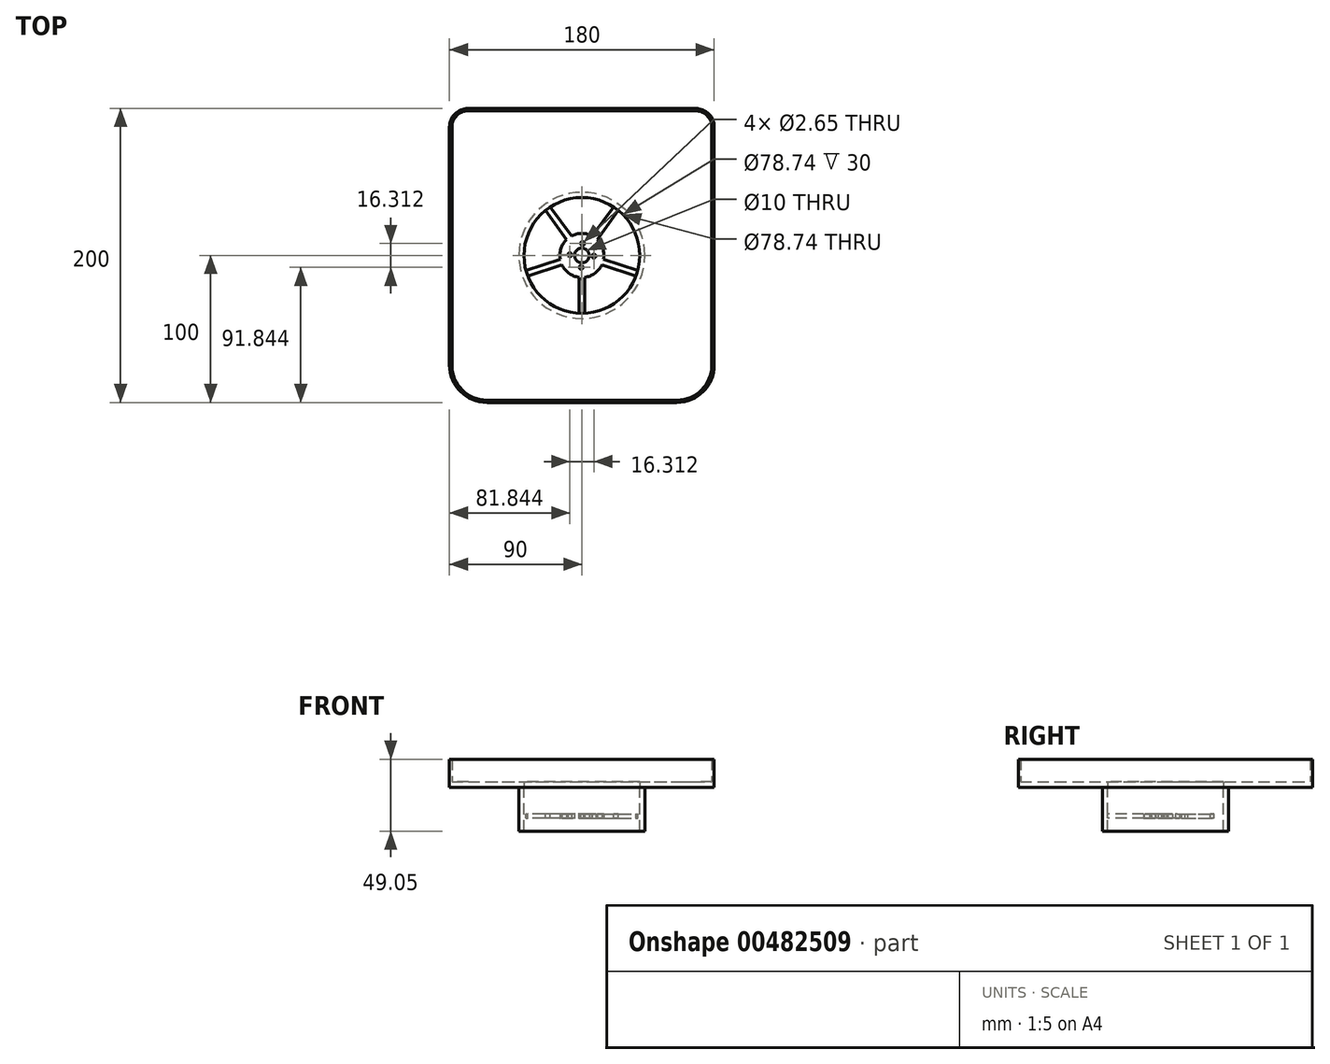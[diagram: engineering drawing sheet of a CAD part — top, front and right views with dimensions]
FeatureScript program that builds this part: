
annotation { "Feature Type Name" : "Feature", "Feature Type Description" : "" }
export const myFeature = defineFeature(function(context is Context, id is Id, definition is map)
    precondition{}
    {
        {
            var Q0;
            Q0=qCreatedBy(makeId("Top.planeOp"),FACE);
            var sketch = newSketch(context, id + "F0", { "sketchPlane" : qUnion([Q0])});
            skLineSegment(sketch, "E0.bottom", {"start": v(25.4, 0) * mm, "end": v(154.6, 0) * mm});
            skLineSegment(sketch, "E0.top", {"start": v(12.7, 200) * mm, "end": v(167.3, 200) * mm});
            skLineSegment(sketch, "E0.left", {"start": v(0, 25.4) * mm, "end": v(0, 187.3) * mm});
            skLineSegment(sketch, "E0.right", {"start": v(180, 25.4) * mm, "end": v(180, 187.3) * mm});
            skPoint(sketch, "E1.visualSharp", {"position": v(0, 0) * mm});
            skArc(sketch, "E1.filletArc", {"start": v(0, 25.4) * mm, "mid": v(7.44, 7.44) * mm, "end": v(25.4, 0) * mm});
            skPoint(sketch, "E2.visualSharp", {"position": v(180, 0) * mm});
            skArc(sketch, "E2.filletArc", {"start": v(154.6, 0) * mm, "mid": v(172.56, 7.44) * mm, "end": v(180, 25.4) * mm});
            skCircle(sketch, "E3", {"center": v(90, 100) * mm, "radius": 39.37 * mm});
            skPoint(sketch, "E4.visualSharp", {"position": v(0, 200) * mm});
            skArc(sketch, "E4.filletArc", {"start": v(12.7, 200) * mm, "mid": v(3.72, 196.28) * mm, "end": v(0, 187.3) * mm});
            skPoint(sketch, "E5.visualSharp", {"position": v(180, 200) * mm});
            skArc(sketch, "E5.filletArc", {"start": v(180, 187.3) * mm, "mid": v(176.28, 196.28) * mm, "end": v(167.3, 200) * mm});
            skSolve(sketch);
        }
        {
            var Q0;
            Q0 = qSketchRegion(id + "F0", true);
            extrude(context, id + "F1", {"entities" : qUnion([Q0]), "depth" : 3.8 * mm});
        }
        {
            var Q0;
            Q0=makeQuery(id+"F1.opExtrude","CAP_FACE",FACE,{"disambiguationData":[OSD([sQuery(id+"F0.wireOp",EDGE,"E0.bottom"),sQuery(id+"F0.wireOp",EDGE,"E0.top"),sQuery(id+"F0.wireOp",EDGE,"E0.left"),sQuery(id+"F0.wireOp",EDGE,"E0.right"),sQuery(id+"F0.wireOp",EDGE,"E1.filletArc"),sQuery(id+"F0.wireOp",EDGE,"E2.filletArc"),sQuery(id+"F0.wireOp",EDGE,"E3"),sQuery(id+"F0.wireOp",EDGE,"E4.filletArc"),sQuery(id+"F0.wireOp",EDGE,"E5.filletArc")])],"isStart":false});
            var sketch = newSketch(context, id + "F2", { "sketchPlane" : qUnion([Q0])});
            skArc(sketch, "E6.0", {"start": v(154.6, 1.6) * mm, "mid": v(171.43, 8.57) * mm, "end": v(178.4, 25.4) * mm});
            skLineSegment(sketch, "E6.1", {"start": v(25.4, 1.6) * mm, "end": v(154.6, 1.6) * mm});
            skLineSegment(sketch, "E6.2", {"start": v(178.4, 25.4) * mm, "end": v(178.4, 187.3) * mm});
            skArc(sketch, "E6.3", {"start": v(1.6, 25.4) * mm, "mid": v(8.57, 8.57) * mm, "end": v(25.4, 1.6) * mm});
            skArc(sketch, "E6.4", {"start": v(178.4, 187.3) * mm, "mid": v(175.15, 195.15) * mm, "end": v(167.3, 198.4) * mm});
            skLineSegment(sketch, "E6.5", {"start": v(12.7, 198.4) * mm, "end": v(167.3, 198.4) * mm});
            skArc(sketch, "E6.6", {"start": v(12.7, 198.4) * mm, "mid": v(4.85, 195.15) * mm, "end": v(1.6, 187.3) * mm});
            skLineSegment(sketch, "E6.7", {"start": v(1.6, 25.4) * mm, "end": v(1.6, 187.3) * mm});
            skSolve(sketch);
        }
        {
            var Q0;
            Q0=makeQuery(id+"F2.imprint","IMPRINT",FACE,{"disambiguationData":[TD([[makeQuery(id+"F2.imprint","IMPRINT",EDGE,{"derivedFrom":sQuery(id+"F2.wireOp",EDGE,"E6.0")}),-1.0]])]});
            extrude(context, id + "F3", {"entities" : qUnion([Q0]), "operationType" : NewBodyOperationType.ADD, "depth" : 15.24 * mm});
        }
        {
            var Q0;
            Q0=qCreatedBy(makeId("Top.planeOp"),FACE);
            var sketch = newSketch(context, id + "F4", { "sketchPlane" : qUnion([Q0])});
            skCircle(sketch, "E7.0", {"center": v(90, 100) * mm, "radius": 42.87 * mm});
            skCircle(sketch, "E8.0", {"center": v(90, 100) * mm, "radius": 39.37 * mm});
            skSolve(sketch);
        }
        {
            var Q0;
            Q0=makeQuery(id+"F4.imprint","IMPRINT",FACE,{"disambiguationData":[TD([[makeQuery(id+"F4.imprint","IMPRINT",EDGE,{"derivedFrom":sQuery(id+"F4.wireOp",EDGE,"E7.0")}),1.0]])]});
            extrude(context, id + "F5", {"entities" : qUnion([Q0]), "oppositeDirection" : true, "depth" : 30 * mm});
        }
        {
            var Q0;
            Q0=makeQuery(id+"F1.opExtrude","CAP_FACE",FACE,{"disambiguationData":[OSD([sQuery(id+"F0.wireOp",EDGE,"E0.bottom"),sQuery(id+"F0.wireOp",EDGE,"E0.top"),sQuery(id+"F0.wireOp",EDGE,"E0.left"),sQuery(id+"F0.wireOp",EDGE,"E0.right"),sQuery(id+"F0.wireOp",EDGE,"E1.filletArc"),sQuery(id+"F0.wireOp",EDGE,"E2.filletArc"),sQuery(id+"F0.wireOp",EDGE,"E3"),sQuery(id+"F0.wireOp",EDGE,"E4.filletArc"),sQuery(id+"F0.wireOp",EDGE,"E5.filletArc")])],"isStart":false});
            cPlane(context, id + "F6", {"entities" : qUnion([Q0]), "cplaneType" : CPlaneType.OFFSET, "offset" : 25 * mm, "oppositeDirection" : true, "width" : 150 * mm, "height" : 150 * mm});
        }
        {
            var Q0;
            Q0=qCreatedBy(id+"F6.planeOp",FACE);
            var sketch = newSketch(context, id + "F7", { "sketchPlane" : qUnion([Q0])});
            skCircle(sketch, "E9", {"center": v(90, 100) * mm, "radius": 5 * mm});
            skCircle(sketch, "E10", {"center": v(90, 100) * mm, "radius": 15 * mm});
            skLineSegment(sketch, "E11.0", {"start": v(88, 86.29) * mm, "end": v(88, 60.55) * mm});
            skLineSegment(sketch, "E12.0", {"start": v(92, 86.13) * mm, "end": v(92, 60.55) * mm});
            skLineSegment(sketch, "E13", {"start": v(88, 86.29) * mm, "end": v(92, 86.13) * mm});
            skLineSegment(sketch, "E14", {"start": v(88, 60.55) * mm, "end": v(92, 60.55) * mm});
            skLineSegment(sketch, "E15.1.0", {"start": v(103.8, 97.62) * mm, "end": v(128.14, 89.71) * mm});
            skLineSegment(sketch, "E15.1.1", {"start": v(102.42, 93.86) * mm, "end": v(126.9, 85.9) * mm});
            skLineSegment(sketch, "E15.1.2", {"start": v(102.42, 93.86) * mm, "end": v(103.8, 97.62) * mm});
            skLineSegment(sketch, "E15.1.3", {"start": v(126.9, 85.9) * mm, "end": v(128.14, 89.71) * mm});
            skLineSegment(sketch, "E15.2.0", {"start": v(96.53, 112.4) * mm, "end": v(111.57, 133.1) * mm});
            skLineSegment(sketch, "E15.2.1", {"start": v(99.68, 109.92) * mm, "end": v(114.8, 130.74) * mm});
            skLineSegment(sketch, "E15.2.2", {"start": v(99.68, 109.92) * mm, "end": v(96.53, 112.4) * mm});
            skLineSegment(sketch, "E15.2.3", {"start": v(114.8, 130.74) * mm, "end": v(111.57, 133.1) * mm});
            skLineSegment(sketch, "E15.3.0", {"start": v(80.23, 110.04) * mm, "end": v(65.2, 130.74) * mm});
            skLineSegment(sketch, "E15.3.1", {"start": v(83.56, 112.27) * mm, "end": v(68.43, 133.1) * mm});
            skLineSegment(sketch, "E15.3.2", {"start": v(83.56, 112.27) * mm, "end": v(80.23, 110.04) * mm});
            skLineSegment(sketch, "E15.3.3", {"start": v(68.43, 133.1) * mm, "end": v(65.2, 130.74) * mm});
            skLineSegment(sketch, "E15.4.0", {"start": v(77.43, 93.81) * mm, "end": v(53.1, 85.9) * mm});
            skLineSegment(sketch, "E15.4.1", {"start": v(76.34, 97.66) * mm, "end": v(51.86, 89.71) * mm});
            skLineSegment(sketch, "E15.4.2", {"start": v(76.34, 97.66) * mm, "end": v(77.43, 93.81) * mm});
            skLineSegment(sketch, "E15.4.3", {"start": v(51.86, 89.71) * mm, "end": v(53.1, 85.9) * mm});
            skSolve(sketch);
        }
        {
            var Q0;
            Q0=makeQuery(id+"F7.imprint","IMPRINT",FACE,{"disambiguationData":[TD([[makeQuery(id+"F7.imprint","IMPRINT",EDGE,{"derivedFrom":sQuery(id+"F7.wireOp",EDGE,"E9")}),-1.0]])]});
            var Q1;
            {var subQ5=sQuery(id+"F7.wireOp",EDGE,"E14");Q1=makeQuery(id+"F7.imprint","IMPRINT",FACE,{"disambiguationData":[TD([[makeQuery(id+"F7.imprint","IMPRINT",EDGE,{"derivedFrom":subQ5}),1.0]])]});}
            var Q2;
            {var subQ5=sQuery(id+"F7.wireOp",EDGE,"E15.4.3");Q2=makeQuery(id+"F7.imprint","IMPRINT",FACE,{"disambiguationData":[TD([[makeQuery(id+"F7.imprint","IMPRINT",EDGE,{"derivedFrom":subQ5}),1.0]])]});}
            var Q3;
            {var subQ5=sQuery(id+"F7.wireOp",EDGE,"E15.3.3");Q3=makeQuery(id+"F7.imprint","IMPRINT",FACE,{"disambiguationData":[TD([[makeQuery(id+"F7.imprint","IMPRINT",EDGE,{"derivedFrom":subQ5}),1.0]])]});}
            var Q4;
            {var subQ5=sQuery(id+"F7.wireOp",EDGE,"E15.2.3");Q4=makeQuery(id+"F7.imprint","IMPRINT",FACE,{"disambiguationData":[TD([[makeQuery(id+"F7.imprint","IMPRINT",EDGE,{"derivedFrom":subQ5}),1.0]])]});}
            var Q5;
            {var subQ5=sQuery(id+"F7.wireOp",EDGE,"E15.1.3");Q5=makeQuery(id+"F7.imprint","IMPRINT",FACE,{"disambiguationData":[TD([[makeQuery(id+"F7.imprint","IMPRINT",EDGE,{"derivedFrom":subQ5}),1.0]])]});}
            var Q6;
            {var subQ5=sQuery(id+"F7.wireOp",EDGE,"E15.1.2");Q6=makeQuery(id+"F7.imprint","IMPRINT",FACE,{"disambiguationData":[TD([[makeQuery(id+"F7.imprint","IMPRINT",EDGE,{"derivedFrom":subQ5}),-1.0]])]});}
            var Q7;
            {var subQ5=sQuery(id+"F7.wireOp",EDGE,"E13");Q7=makeQuery(id+"F7.imprint","IMPRINT",FACE,{"disambiguationData":[TD([[makeQuery(id+"F7.imprint","IMPRINT",EDGE,{"derivedFrom":subQ5}),-1.0]])]});}
            var Q8;
            {var subQ5=sQuery(id+"F7.wireOp",EDGE,"E15.4.2");Q8=makeQuery(id+"F7.imprint","IMPRINT",FACE,{"disambiguationData":[TD([[makeQuery(id+"F7.imprint","IMPRINT",EDGE,{"derivedFrom":subQ5}),-1.0]])]});}
            var Q9;
            {var subQ5=sQuery(id+"F7.wireOp",EDGE,"E15.3.2");Q9=makeQuery(id+"F7.imprint","IMPRINT",FACE,{"disambiguationData":[TD([[makeQuery(id+"F7.imprint","IMPRINT",EDGE,{"derivedFrom":subQ5}),-1.0]])]});}
            var Q10;
            {var subQ5=sQuery(id+"F7.wireOp",EDGE,"E15.2.2");Q10=makeQuery(id+"F7.imprint","IMPRINT",FACE,{"disambiguationData":[TD([[makeQuery(id+"F7.imprint","IMPRINT",EDGE,{"derivedFrom":subQ5}),-1.0]])]});}
            extrude(context, id + "F8", {"entities" : qUnion([Q0, Q1, Q2, Q3, Q4, Q5, Q6, Q7, Q8, Q9, Q10]), "operationType" : NewBodyOperationType.ADD, "depth" : 3 * mm});
        }
        {
            var Q0;
            Q0=makeQuery(id+"F8.opExtrude","CAP_FACE",FACE,{"disambiguationData":[OSD([sQuery(id+"F7.wireOp",EDGE,"E9"),sQuery(id+"F7.wireOp",EDGE,"E10"),sQuery(id+"F7.wireOp",EDGE,"E11.0"),sQuery(id+"F7.wireOp",EDGE,"E12.0"),sQuery(id+"F7.wireOp",EDGE,"E14"),sQuery(id+"F7.wireOp",EDGE,"E15.1.0"),sQuery(id+"F7.wireOp",EDGE,"E15.1.1"),sQuery(id+"F7.wireOp",EDGE,"E15.1.3"),sQuery(id+"F7.wireOp",EDGE,"E15.2.0"),sQuery(id+"F7.wireOp",EDGE,"E15.2.1"),sQuery(id+"F7.wireOp",EDGE,"E15.2.3"),sQuery(id+"F7.wireOp",EDGE,"E15.3.0"),sQuery(id+"F7.wireOp",EDGE,"E15.3.1"),sQuery(id+"F7.wireOp",EDGE,"E15.3.3"),sQuery(id+"F7.wireOp",EDGE,"E15.4.0"),sQuery(id+"F7.wireOp",EDGE,"E15.4.1"),sQuery(id+"F7.wireOp",EDGE,"E15.4.3")])],"isStart":true});
            var sketch = newSketch(context, id + "F9", { "sketchPlane" : qUnion([Q0])});
            skCircle(sketch, "E16", {"center": v(90.47, -108.16) * mm, "radius": 1.33 * mm});
            skCircle(sketch, "E17.1.0", {"center": v(98.16, -99.53) * mm, "radius": 1.33 * mm});
            skCircle(sketch, "E17.2.0", {"center": v(89.53, -91.84) * mm, "radius": 1.33 * mm});
            skCircle(sketch, "E17.3.0", {"center": v(81.84, -100.47) * mm, "radius": 1.33 * mm});
            skPoint(sketch, "E17.center", {"position": v(90, -100) * mm});
            skSolve(sketch);
        }
        {
            var Q0;
            Q0=makeQuery(id+"F9.imprint","IMPRINT",FACE,{"disambiguationData":[TD([[makeQuery(id+"F9.imprint","IMPRINT",EDGE,{"derivedFrom":sQuery(id+"F9.wireOp",EDGE,"E16")}),1.0]])]});
            var Q1;
            Q1=makeQuery(id+"F9.imprint","IMPRINT",FACE,{"disambiguationData":[TD([[makeQuery(id+"F9.imprint","IMPRINT",EDGE,{"derivedFrom":sQuery(id+"F9.wireOp",EDGE,"E17.1.0")}),1.0]])]});
            var Q2;
            Q2=makeQuery(id+"F9.imprint","IMPRINT",FACE,{"disambiguationData":[TD([[makeQuery(id+"F9.imprint","IMPRINT",EDGE,{"derivedFrom":sQuery(id+"F9.wireOp",EDGE,"E17.2.0")}),1.0]])]});
            var Q3;
            Q3=makeQuery(id+"F9.imprint","IMPRINT",FACE,{"disambiguationData":[TD([[makeQuery(id+"F9.imprint","IMPRINT",EDGE,{"derivedFrom":sQuery(id+"F9.wireOp",EDGE,"E17.3.0")}),1.0]])]});
            extrude(context, id + "F10", {"entities" : qUnion([Q0, Q1, Q2, Q3]), "operationType" : NewBodyOperationType.REMOVE, "oppositeDirection" : true, "depth" : 25 * mm});
        }
    });
